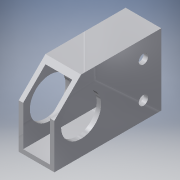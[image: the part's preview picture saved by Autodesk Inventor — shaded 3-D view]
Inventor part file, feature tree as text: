
AUTODESK INVENTOR PART (.ipt)
format: ipt  version: 2016 (Build 200138000, 138)  size: 145,408 bytes
history: native  units: in
note: dims shown in document units (in); Inventor stores cm internally (conversion verified against a paired STEP export)
features: extrude x4, sketch x4
ambient origin geometry x8: Origin, YZ Plane, XZ Plane, XY Plane, X Axis, Y Axis, Z Axis, Center Point
bodies: Solid1 (feature_tree)
feature tree (8):
  extrude  "Extrusion1"  Depth=2.0in
  extrude  "Extrusion2"  Depth=0.125in
  extrude  "Extrusion3"  Depth=0.125in
  extrude  "Extrusion4"  Depth=1.0in
  sketch  "Sketch1"  dims[d0=1.0in d1=2.0in]
  sketch  "Sketch2"  dims[d2=0.125in d3=0.125in]
  sketch  "Sketch3"  dims[d4=0.125in d5=0.125in]
  sketch  "Sketch4"  dims[d6=3.0in d7=0.0in d8=1.125in d9=0.75in d10=1.0in d11=3.0in d12=0.0in d13=135.0deg d14=0.75in d15=3.0in d16=0.0in d17=0.2656in d18=0.5in d19=1.5in d20=0.5in d21=0.5in d22=1.0in d23=0.0in]
